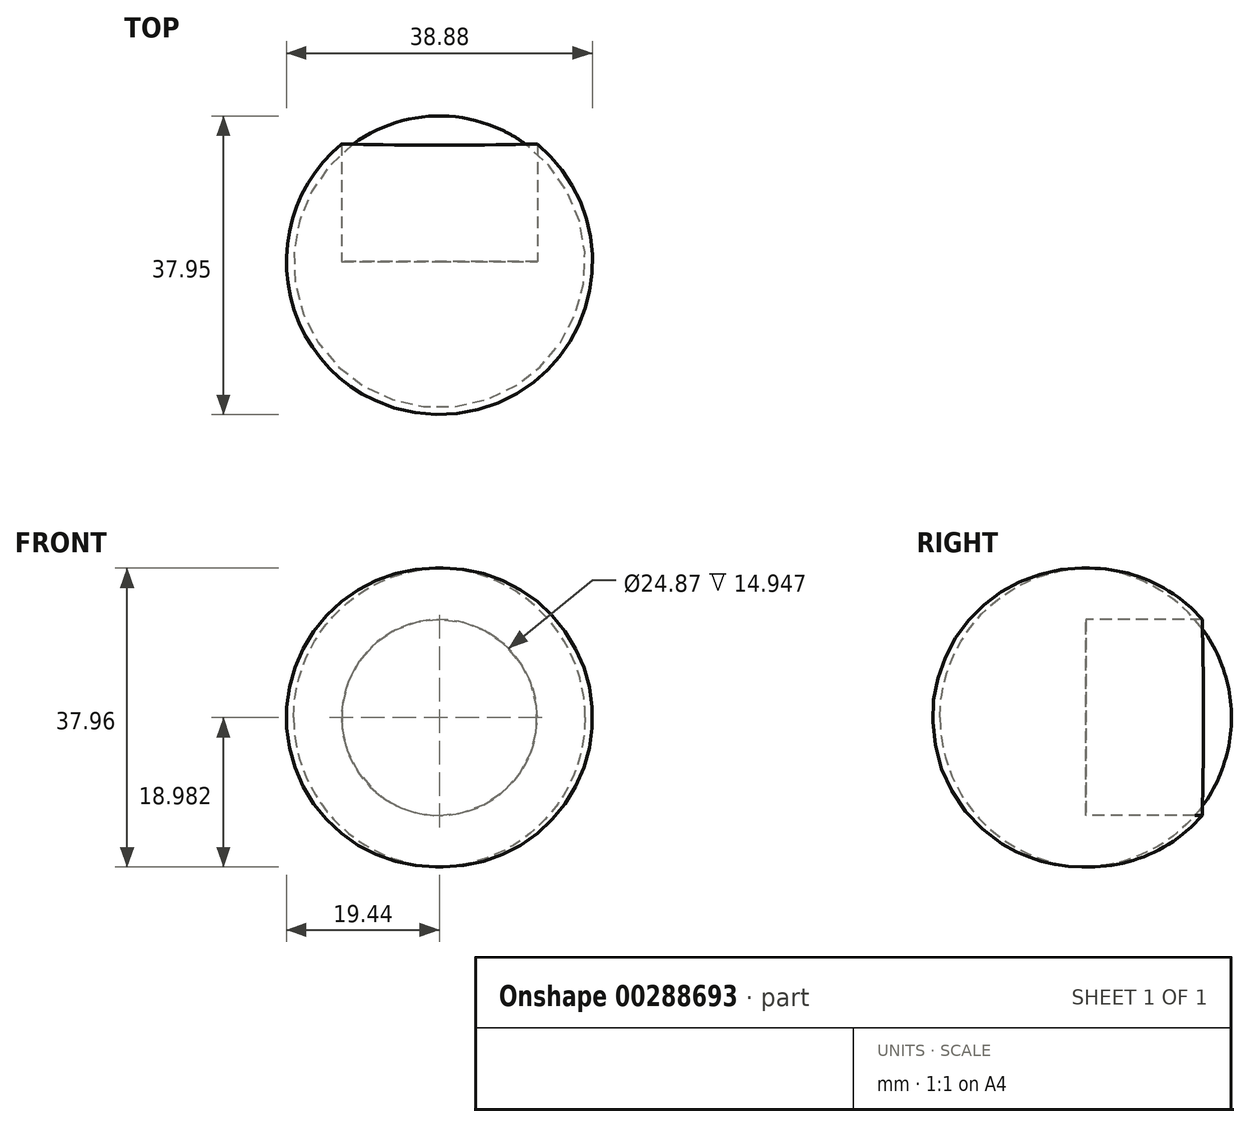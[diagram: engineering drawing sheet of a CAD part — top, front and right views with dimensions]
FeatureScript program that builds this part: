
annotation { "Feature Type Name" : "Feature", "Feature Type Description" : "" }
export const myFeature = defineFeature(function(context is Context, id is Id, definition is map)
    precondition{}
    {
        {
            var Q0;
            Q0=qCreatedBy(makeId("Front.planeOp"),FACE);
            var sketch = newSketch(context, id + "F0", { "sketchPlane" : qUnion([Q0])});
            skLineSegment(sketch, "E0", {"start": v(0, 37.94) * mm, "end": v(0, 0) * mm});
            skArc(sketch, "E1", {"start": v(0, 0) * mm, "mid": v(19.44, 18.97) * mm, "end": v(0, 37.94) * mm});
            skSolve(sketch);
        }
        {
            var Q0;
            Q0 = qSketchRegion(id + "F0", true);
            var Q1;
            Q1=sQuery(id+"F0.wireOp",EDGE,"E0");
            revolve(context, id + "F1", {"entities" : qUnion([Q0]), "axis" : qUnion([Q1]), "revolveType" : RevolveType.FULL});
        }
        {
            var Q0;
            Q0=qCreatedBy(makeId("Front.planeOp"),FACE);
            var sketch = newSketch(context, id + "F2", { "sketchPlane" : qUnion([Q0])});
            skCircle(sketch, "E2", {"center": v(0, 18.97) * mm, "radius": 12.43 * mm});
            skSolve(sketch);
        }
        {
            var Q0;
            Q0 = qSketchRegion(id + "F2", true);
            extrude(context, id + "F3", {"entities" : qUnion([Q0]), "operationType" : NewBodyOperationType.REMOVE, "oppositeDirection" : true, "depth" : 25.4 * mm});
        }
    });
